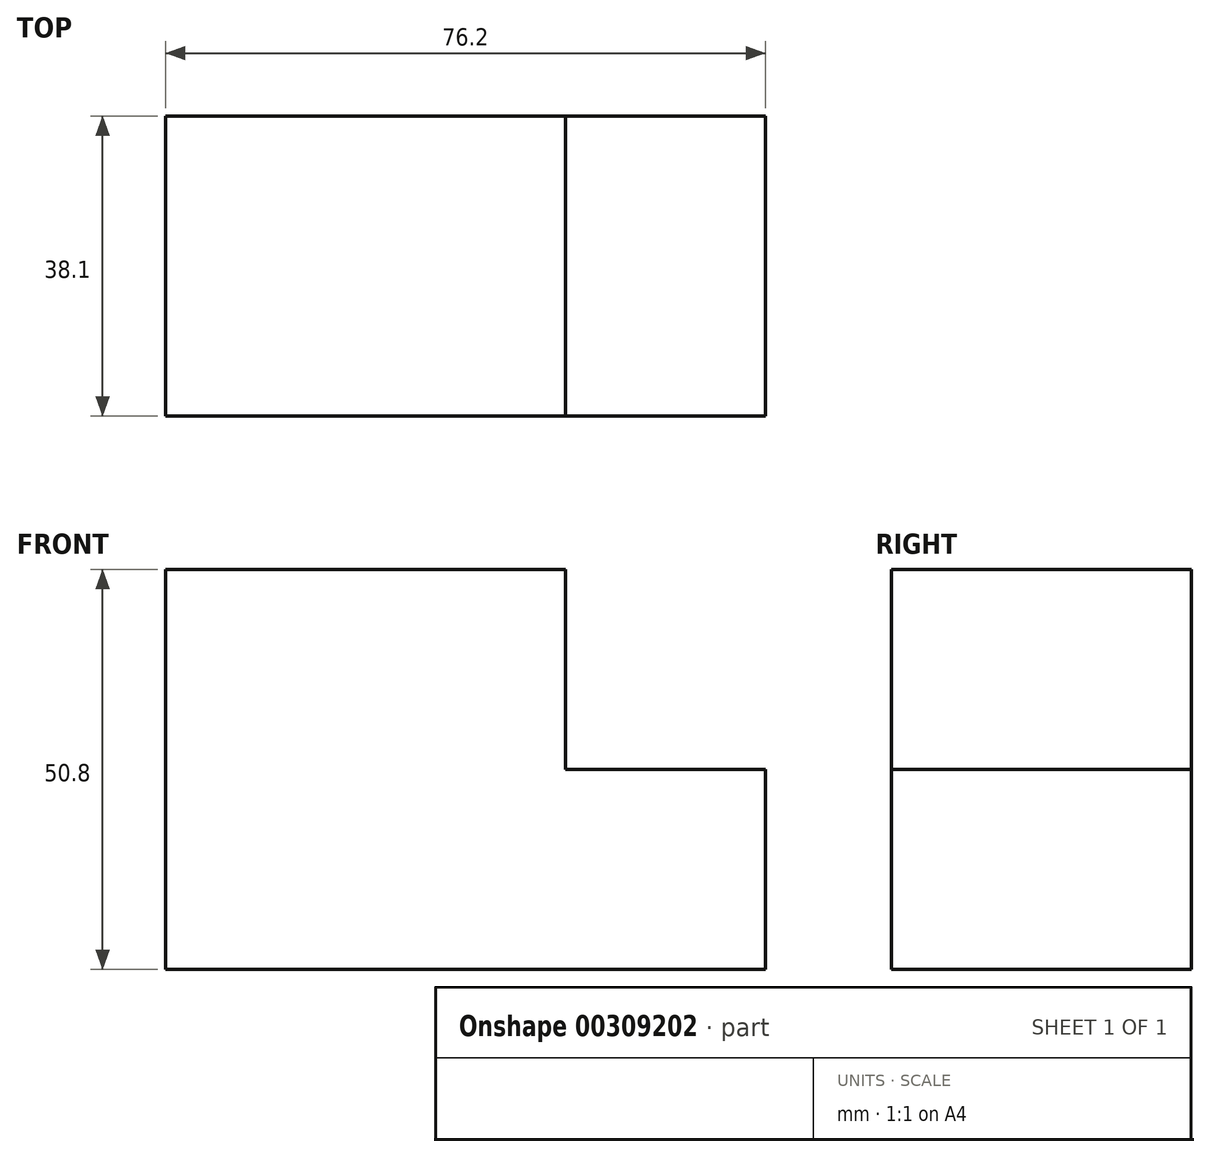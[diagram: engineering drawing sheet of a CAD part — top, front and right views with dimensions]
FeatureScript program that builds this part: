
annotation { "Feature Type Name" : "Feature", "Feature Type Description" : "" }
export const myFeature = defineFeature(function(context is Context, id is Id, definition is map)
    precondition{}
    {
        {
            var Q0;
            Q0=qCreatedBy(makeId("Front.planeOp"),FACE);
            var sketch = newSketch(context, id + "F0", { "sketchPlane" : qUnion([Q0])});
            skLineSegment(sketch, "E0", {"start": v(-37.7, -42.08) * mm, "end": v(38.5, -42.08) * mm});
            skLineSegment(sketch, "E1", {"start": v(38.5, -42.08) * mm, "end": v(38.5, -16.68) * mm});
            skLineSegment(sketch, "E2", {"start": v(38.5, -16.68) * mm, "end": v(13.1, -16.68) * mm});
            skLineSegment(sketch, "E3", {"start": v(13.1, -16.68) * mm, "end": v(13.1, 8.72) * mm});
            skLineSegment(sketch, "E4", {"start": v(13.1, 8.72) * mm, "end": v(-37.7, 8.72) * mm});
            skLineSegment(sketch, "E5", {"start": v(-37.7, 8.72) * mm, "end": v(-37.7, -42.08) * mm});
            skSolve(sketch);
        }
        {
            var Q0;
            Q0=makeQuery(id+"F0.imprint","IMPRINT",FACE,{"disambiguationData":[TD([[makeQuery(id+"F0.imprint","IMPRINT",EDGE,{"derivedFrom":sQuery(id+"F0.wireOp",EDGE,"E0")}),1.0]])]});
            extrude(context, id + "F1", {"entities" : qUnion([Q0]), "depth" : 38.1 * mm});
        }
    });
